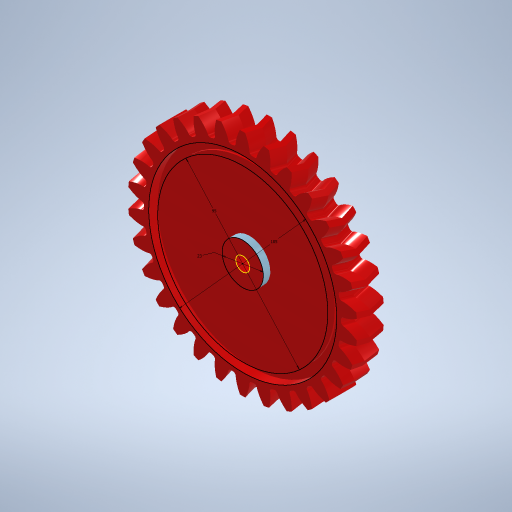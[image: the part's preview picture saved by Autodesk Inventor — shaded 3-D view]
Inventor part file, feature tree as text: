
AUTODESK INVENTOR PART (.ipt)
format: ipt  version: 2024.2 (Build 282272000, 272)  size: 2,075,136 bytes
history: native  units: mm
features: other x4, extrude x3, sketch x2
ambient origin geometry x8: Origin, YZ Plane, XZ Plane, XY Plane, X Axis, Y Axis, Z Axis, Center Point
bodies: Body1 (feature_tree)
feature tree (9):
  other  "Bryła1"
  sketch  "Szkic1"
  extrude  "Wyciągnięcie proste1"  Depth=105.0mm
  extrude  "Wyciągnięcie proste2"  Depth=95.0mm
  extrude  "Wyciągnięcie proste6"  Depth=5.0mm TaperAngle=0.0deg
  sketch  "Szkic2"
  other  "Spur gear (30 teeth)"
  other  "Finish1"
  other  "Finish2"
